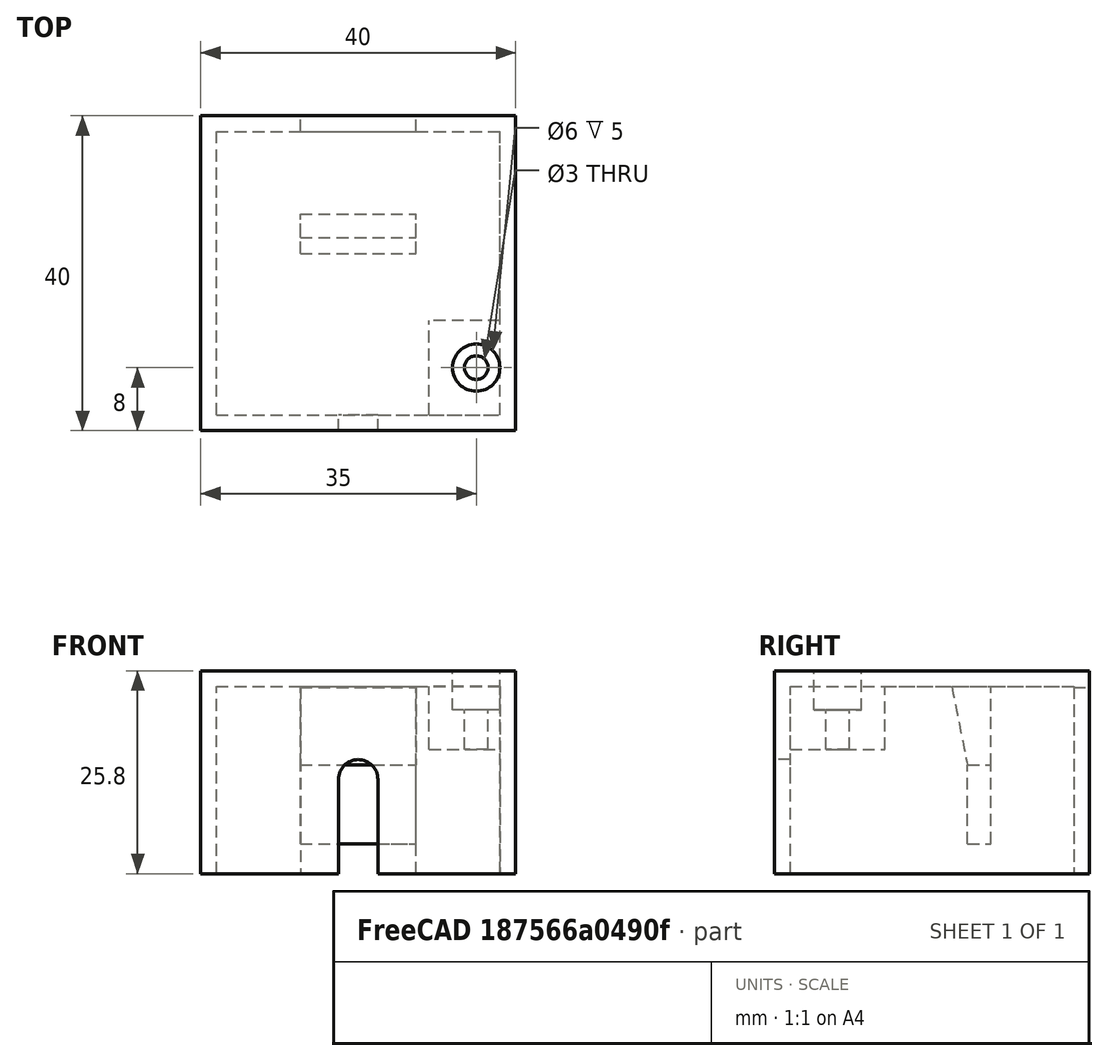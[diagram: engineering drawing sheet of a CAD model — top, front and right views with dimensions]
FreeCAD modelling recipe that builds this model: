
FCSTD DOCUMENT  (FreeCAD 0.19R24291 (Git))
Label: eth_conn_top_1
License: All rights reserved
LicenseURL: http://en.wikipedia.org/wiki/All_rights_reserved
objects: Part::Box×7, Part::Cut×6, Part::Cylinder×3, Part::FeaturePython×2, Part::Feature×1, Part::Extrusion×1, Surface::GeomFillSurface×1, Part::MultiFuse×1, App::DocumentObjectGroup×1, Part::Refine×1
note: 23 computed .brp shape members not serialized (recipe doc carries the construction recipe); baked Part::Feature solids carry a one-line shape summary decoded from their .brp

FEATURE [Part::Box] Box  label="Cube"
  AttacherType = Attacher::AttachEngine3D
  Height = 25.5
  Length = 40
  Placement = pos=(-20,0,0) rot=(0,0,1;0rad)
  Width = 40
FEATURE [Part::Box] Box001  label="Cube001"
  AttacherType = Attacher::AttachEngine3D
  Height = 23.5
  Length = 36
  Placement = pos=(-18,2,0) rot=(0,0,1;0rad)
  Width = 36
FEATURE [Part::Cut] Cut
  Base = -> Box
  Placement = pos=(0,0,0.3) rot=(0,0,1;0rad)
  Tool = -> Box001
FEATURE [Part::Box] Box002  label="Cube002"
  AttacherType = Attacher::AttachEngine3D
  Height = 12
  Length = 5
  Placement = pos=(-2.5,0,0) rot=(0,0,1;0rad)
  Width = 3
FEATURE [Part::Cylinder] Cylinder
  Angle = 360
  AttacherType = Attacher::AttachEngine3D
  Height = 3
  Placement = pos=(0,3,12) rot=(1,0,0;1.5708rad)
  Radius = 2.5
FEATURE [Part::Box] Box003  label="Cube003"
  AttacherType = Attacher::AttachEngine3D
  Height = 23.7
  Length = 14.7
  Placement = pos=(-7.35,37,0) rot=(0,0,1;0rad)
  Width = 3
FEATURE [Part::Feature] Face
  Placement = pos=(0,0,0.3) rot=(0,0,1;0rad)
  shape: bbox 40 x 40 x 2e-07 mm, 1 faces, 0 solids (baked)
FEATURE [Part::Extrusion] Extrusion
  Base = -> Face
  Dir = (0,0,-0.3)
  DirMode = 0
  FaceMakerClass = Part::FaceMakerBullseye
  LengthFwd = 0
  LengthRev = 0
  Solid = true
  Symmetric = false
FEATURE [Part::Box] Box004  label="Cube004"
  AttacherType = Attacher::AttachEngine3D
  Height = 10
  Length = 14.7
  Placement = pos=(-7.35,22.5,13.8) rot=(0,0,1;0rad)
  Width = 5
FEATURE [Part::Box] Box005  label="Cube005"
  AttacherType = Attacher::AttachEngine3D
  Height = 10
  Length = 14.7
  Placement = pos=(-7.35,24.5,3.8) rot=(0,0,1;0rad)
  Width = 3
FEATURE [Surface::GeomFillSurface] Surface
  BoundaryList = -> [Box004,Box005]
  FillType = 0
FEATURE [Part::Cylinder] Cylinder001
  Angle = 360
  AttacherType = Attacher::AttachEngine3D
  Height = 5
  Placement = pos=(15,8,20.8) rot=(0,0,1;0rad)
  Radius = 3
FEATURE [Part::Box] Box006  label="Cube006"
  AttacherType = Attacher::AttachEngine3D
  Height = 10
  Length = 9
  Placement = pos=(9,2,15.8) rot=(0,0,1;0rad)
  Width = 12
FEATURE [Part::Cylinder] Cylinder002
  Angle = 360
  AttacherType = Attacher::AttachEngine3D
  Height = 10
  Placement = pos=(15,8,15.8) rot=(0,0,1;0rad)
  Radius = 1.5
FEATURE [Part::FeaturePython] Slice  # WARN: FeaturePython — macro-defined, semantics opaque (R4)
  Base = -> Box004
  Mode = 1
  Tolerance = 0
  Tools = -> [Surface]
FEATURE [Part::FeaturePython] Slice_child1  label="Slice.1"  # WARN: FeaturePython — macro-defined, semantics opaque (R4)
  Base = -> Slice
  FilterType = 1
  Invert = false
  OverrideMaxVal = 0
  WindowFrom = 80
  WindowTo = 100
  items = 1
FEATURE [Part::MultiFuse] Fusion
  Shapes = -> [Cut,Extrusion,Slice_child1,Box006]
FEATURE [Part::Cut] Cut001
  Base = -> Fusion
  Tool = -> Box002
FEATURE [Part::Cut] Cut002
  Base = -> Cut001
  Tool = -> Cylinder
FEATURE [Part::Cut] Cut003
  Base = -> Cut002
  Tool = -> Box003
FEATURE [Part::Cut] Cut004
  Base = -> Cut003
  Tool = -> Cylinder001
FEATURE [Part::Cut] Cut005
  Base = -> Cut004
  Tool = -> Cylinder002
FEATURE [App::DocumentObjectGroup] GrExplode_Slice  label="Exploded Slice"
  Group = -> [Cut005]
FEATURE [Part::Refine] Cut005001
  Source = -> Cut005
